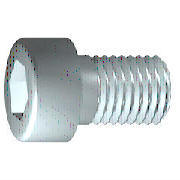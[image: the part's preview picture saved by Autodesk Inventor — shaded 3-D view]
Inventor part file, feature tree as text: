
AUTODESK INVENTOR PART (.ipt)
format: ipt  version: 2019 (Build 230136000, 136)  size: 193,024 bytes
history: native  units: mm (DEFAULTED — no unit token found)
features: sketch x2, extrude x1, plane x1, fillet x1
ambient origin geometry x7: Origin, YZ Plane, XY Plane, X Axis, Y Axis, Z Axis, Center Point
bodies: Solid1 (feature_tree), Body (feature_tree)
feature tree (5):
  extrude  "Slot"  Depth=5.0mm
  plane  "Work Plane1"
  fillet  "Fillet2"  Radius=5.0mm
  sketch  "Sketch1"  dims[d1=23.0mm d2=0.49086mm d3=5.0mm]
  sketch  "Sketch2"  dims[d4=2.5mm d5=60.0deg d6=5.0mm d7=5.0mm d8=4.618802mm d9=8.5mm d10=90.0deg d11=10.0mm d12=0.0mm d13=23.0mm d14=0.0mm d15=0.49076mm d16=0.49076mm d17=0.5mm d19=0.0mm d26=25.0mm d27=45.0deg d28=0.0mm d29=0.0mm d30=0.1mm]
